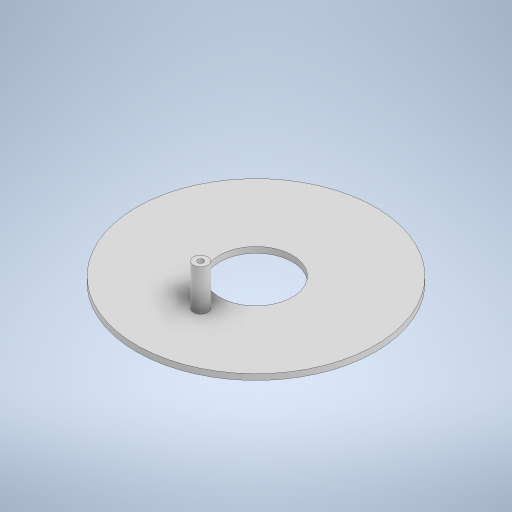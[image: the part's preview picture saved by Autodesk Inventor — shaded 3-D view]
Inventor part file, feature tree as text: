
AUTODESK INVENTOR PART (.ipt)
format: ipt  version: 2024 (Build 280153000, 153)  size: 238,080 bytes
history: native  units: in
note: dims shown in document units (in); Inventor stores cm internally (conversion verified against a paired STEP export)
features: extrude x3, sketch x3
ambient origin geometry x8: Origin, YZ Plane, XZ Plane, XY Plane, X Axis, Y Axis, Z Axis, Center Point
bodies: Solid1 (feature_tree)
feature tree (6):
  extrude  "Extrusion1"  Depth=0.9843in
  extrude  "Extrusion2"  Depth=0.0787in
  extrude  "Extrusion3"  Depth=0.5512in
  sketch  "Sketch1"  dims[d0=3.2283in d1=0.9843in]
  sketch  "Sketch2"  dims[d2=0.0787in d3=0.0in d4=0.748in]
  sketch  "Sketch3"  dims[d5=90.0deg d6=0.1969in d7=0.5512in d8=0.0in d9=0.0787in d10=0.5512in d11=0.0in]
